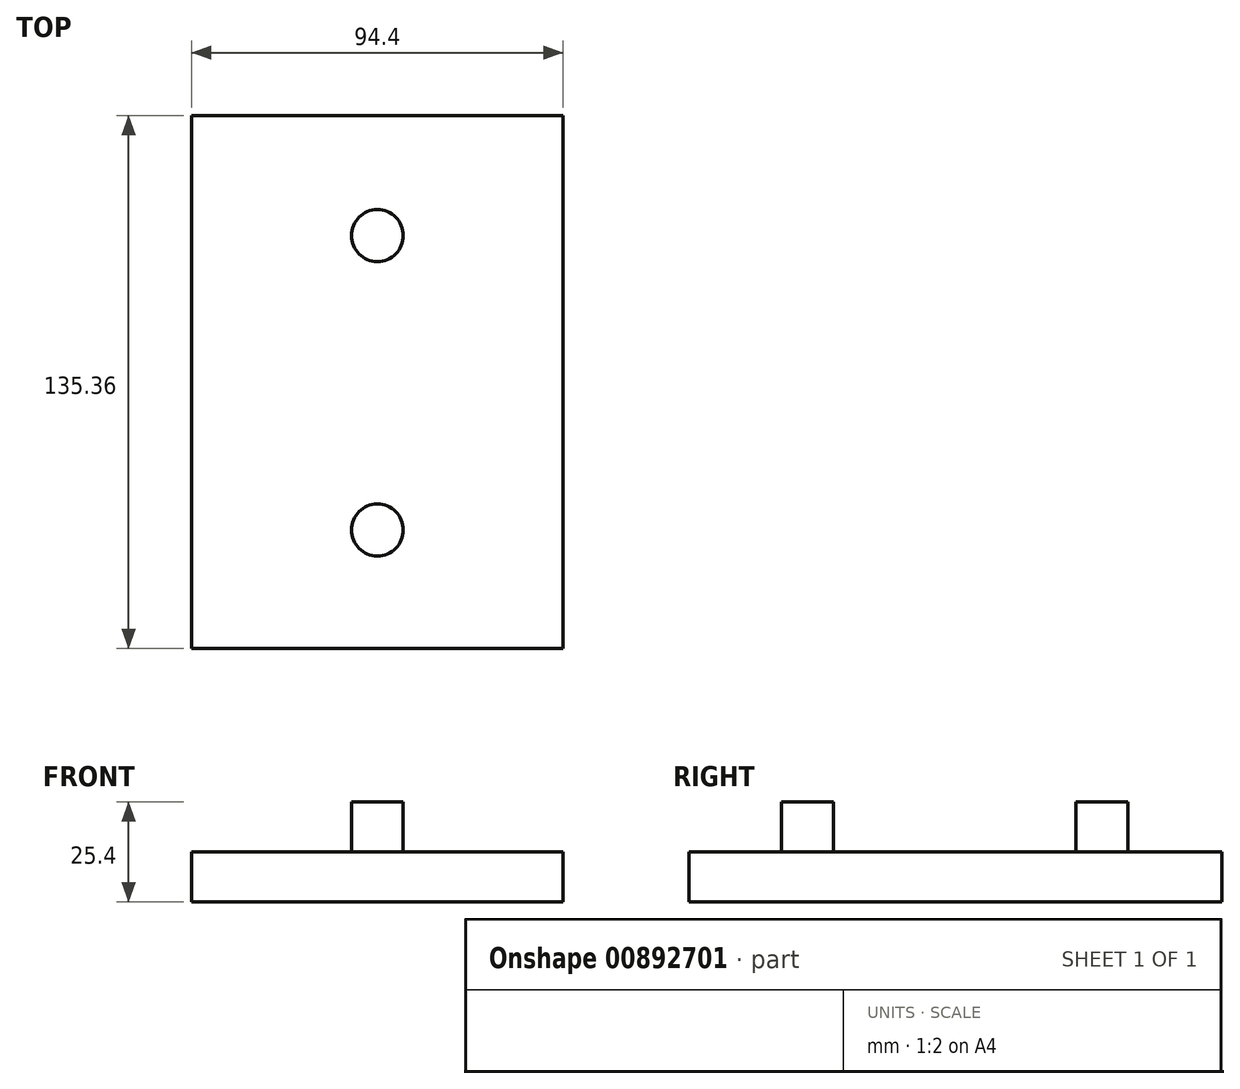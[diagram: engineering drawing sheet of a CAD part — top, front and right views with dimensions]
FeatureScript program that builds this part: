
annotation { "Feature Type Name" : "Feature", "Feature Type Description" : "" }
export const myFeature = defineFeature(function(context is Context, id is Id, definition is map)
    precondition{}
    {
        {
            var Q0;
            Q0=qCreatedBy(makeId("Top.planeOp"),FACE);
            var sketch = newSketch(context, id + "F0", { "sketchPlane" : qUnion([Q0])});
            skLineSegment(sketch, "E0.bottom", {"start": v(-47.2, 50.23) * mm, "end": v(0, 50.23) * mm});
            skLineSegment(sketch, "E0.top", {"start": v(-47.2, -85.13) * mm, "end": v(0, -85.13) * mm});
            skLineSegment(sketch, "E0.left", {"start": v(-47.2, 50.23) * mm, "end": v(-47.2, 19.75) * mm});
            skLineSegment(sketch, "E0.right", {"start": v(47.2, 50.23) * mm, "end": v(47.2, 19.75) * mm});
            skCircle(sketch, "E1", {"center": v(0, -55.05) * mm, "radius": 6.59 * mm});
            skCircle(sketch, "E2", {"center": v(0, 19.75) * mm, "radius": 6.59 * mm});
            skLineSegment(sketch, "E3", {"start": v(-47.2, 19.75) * mm, "end": v(-47.2, -54.65) * mm});
            skLineSegment(sketch, "E4", {"start": v(-47.2, -54.65) * mm, "end": v(-47.2, -85.13) * mm});
            skLineSegment(sketch, "E5", {"start": v(47.2, 19.75) * mm, "end": v(47.2, -54.65) * mm});
            skLineSegment(sketch, "E6", {"start": v(47.2, -54.65) * mm, "end": v(47.2, -85.13) * mm});
            skLineSegment(sketch, "E7", {"start": v(0, 50.23) * mm, "end": v(47.2, 50.23) * mm});
            skLineSegment(sketch, "E8", {"start": v(0, -85.13) * mm, "end": v(47.2, -85.13) * mm});
            skSolve(sketch);
        }
        {
            var Q0;
            Q0 = qSketchRegion(id + "F0", true);
            var Q1;
            Q1=makeQuery(id+"F0.imprint","IMPRINT",FACE,{"disambiguationData":[TD([[makeQuery(id+"F0.imprint","IMPRINT",EDGE,{"derivedFrom":sQuery(id+"F0.wireOp",EDGE,"E2")}),1.0]])]});
            var Q2;
            Q2=makeQuery(id+"F0.imprint","IMPRINT",FACE,{"disambiguationData":[TD([[makeQuery(id+"F0.imprint","IMPRINT",EDGE,{"derivedFrom":sQuery(id+"F0.wireOp",EDGE,"E1")}),1.0]])]});
            extrude(context, id + "F1", {"entities" : qUnion([Q0, Q1, Q2]), "depth" : 12.7 * mm, "offsetDistance" : 25.4 * mm});
        }
        {
            var Q0;
            Q0=makeQuery(id+"F0.imprint","IMPRINT",FACE,{"disambiguationData":[TD([[makeQuery(id+"F0.imprint","IMPRINT",EDGE,{"derivedFrom":sQuery(id+"F0.wireOp",EDGE,"E2")}),1.0]])]});
            var Q1;
            Q1=makeQuery(id+"F0.imprint","IMPRINT",FACE,{"disambiguationData":[TD([[makeQuery(id+"F0.imprint","IMPRINT",EDGE,{"derivedFrom":sQuery(id+"F0.wireOp",EDGE,"E1")}),1.0]])]});
            extrude(context, id + "F2", {"entities" : qUnion([Q0, Q1]), "operationType" : NewBodyOperationType.ADD, "depth" : 25.4 * mm, "offsetDistance" : 25.4 * mm});
        }
    });
